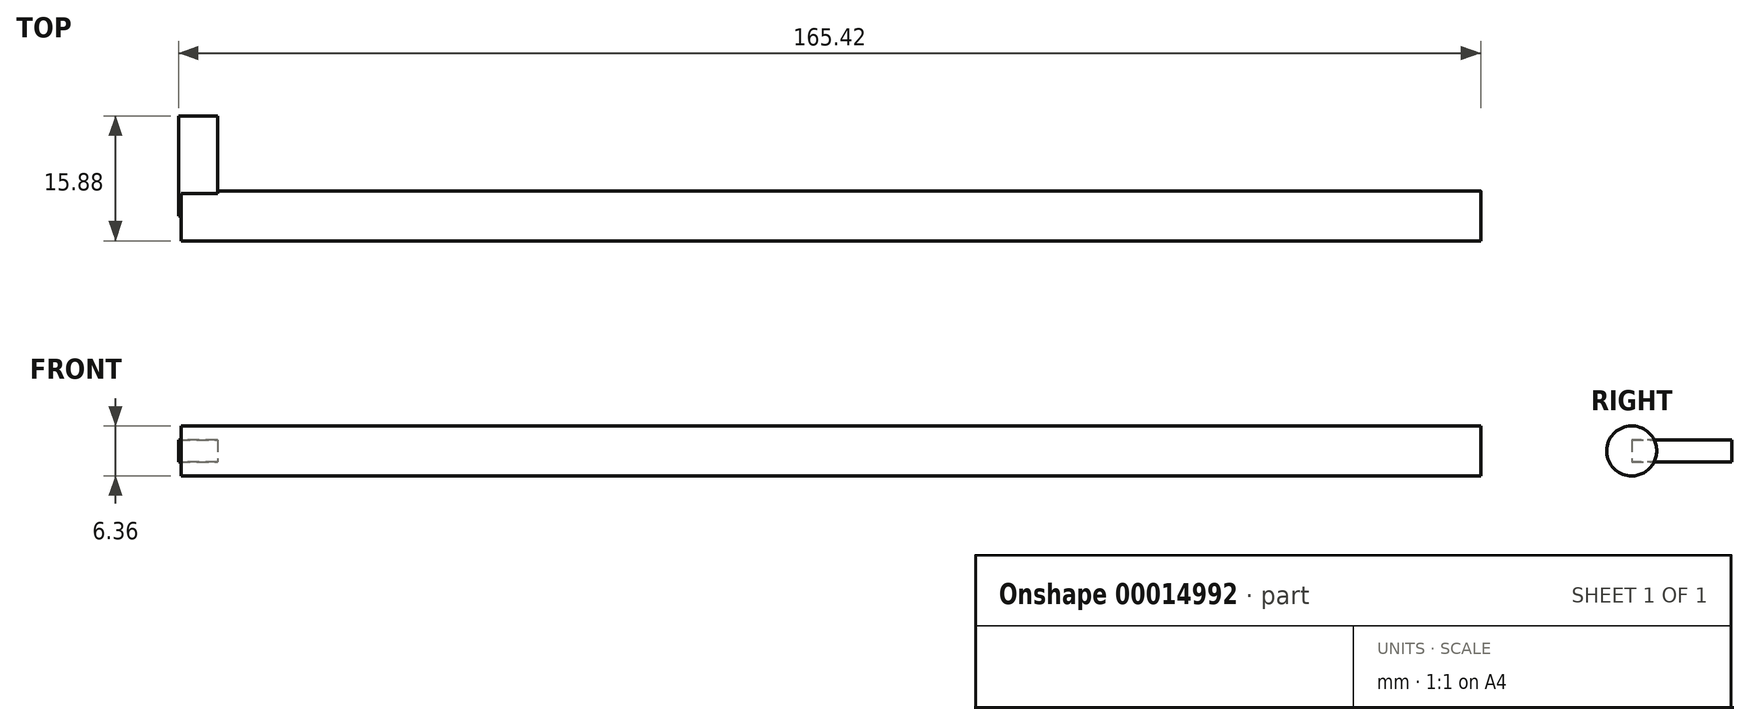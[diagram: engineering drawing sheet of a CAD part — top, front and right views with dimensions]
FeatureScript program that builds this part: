
annotation { "Feature Type Name" : "Feature", "Feature Type Description" : "" }
export const myFeature = defineFeature(function(context is Context, id is Id, definition is map)
    precondition{}
    {
        {
            var Q0;
            Q0=qCreatedBy(makeId("Right.planeOp"),FACE);
            var sketch = newSketch(context, id + "F0", { "sketchPlane" : qUnion([Q0])});
            skCircle(sketch, "E0", {"center": v(0, 0) * mm, "radius": 3.18 * mm});
            skSolve(sketch);
        }
        {
            var Q0;
            Q0=makeQuery(id+"F0.imprint","IMPRINT",FACE,{"disambiguationData":[TD([[makeQuery(id+"F0.imprint","IMPRINT",EDGE,{"derivedFrom":sQuery(id+"F0.wireOp",EDGE,"E0")}),1.0]])]});
            extrude(context, id + "F1", {"entities" : qUnion([Q0]), "depth" : 76.2 * mm});
        }
        {
            var Q0;
            Q0=makeQuery(id+"F1.opExtrude","CAP_FACE",FACE,{"disambiguationData":[OSD([sQuery(id+"F0.wireOp",EDGE,"E0")])],"isStart":true});
            extrude(context, id + "F2", {"entities" : qUnion([Q0]), "operationType" : NewBodyOperationType.ADD, "depth" : 88.9 * mm});
        }
        {
            var Q0;
            Q0=qCreatedBy(makeId("Front.planeOp"),FACE);
            var sketch = newSketch(context, id + "F3", { "sketchPlane" : qUnion([Q0])});
            skLineSegment(sketch, "E1.rect.bottom", {"start": v(-89.22, 1.38) * mm, "end": v(-84.27, 1.38) * mm});
            skLineSegment(sketch, "E1.rect.top", {"start": v(-89.22, -1.38) * mm, "end": v(-84.27, -1.38) * mm});
            skLineSegment(sketch, "E1.rect.left", {"start": v(-89.22, 1.38) * mm, "end": v(-89.22, -1.38) * mm});
            skLineSegment(sketch, "E1.rect.right", {"start": v(-84.27, 1.38) * mm, "end": v(-84.27, -1.38) * mm});
            skPoint(sketch, "E1.rect.middle", {"position": v(-86.75, 0) * mm});
            skSolve(sketch);
        }
        {
            var Q0;
            Q0=makeQuery(id+"F3.imprint","IMPRINT",FACE,{"disambiguationData":[TD([[makeQuery(id+"F3.imprint","IMPRINT",EDGE,{"derivedFrom":sQuery(id+"F3.wireOp",EDGE,"E1.rect.bottom")}),-1.0]])]});
            extrude(context, id + "F4", {"entities" : qUnion([Q0]), "operationType" : NewBodyOperationType.ADD, "oppositeDirection" : true, "depth" : 12.7 * mm});
        }
    });
